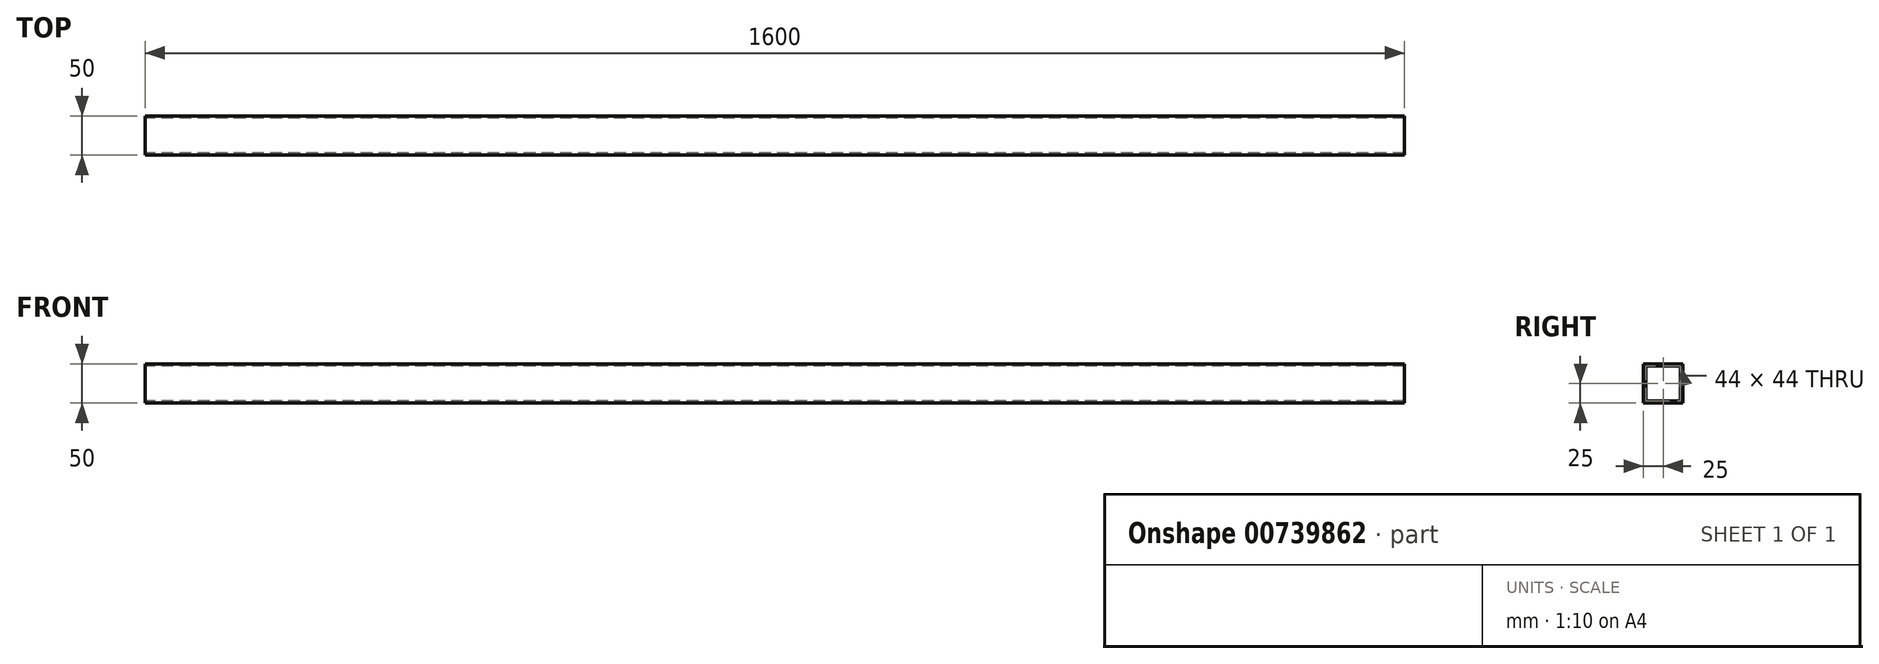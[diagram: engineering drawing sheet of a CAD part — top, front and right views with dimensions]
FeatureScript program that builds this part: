
annotation { "Feature Type Name" : "Feature", "Feature Type Description" : "" }
export const myFeature = defineFeature(function(context is Context, id is Id, definition is map)
    precondition{}
    {
        {
            var Q0;
            Q0=qCreatedBy(makeId("Right.planeOp"),FACE);
            var sketch = newSketch(context, id + "F0", { "sketchPlane" : qUnion([Q0])});
            skLineSegment(sketch, "E0.bottom", {"start": v(25, -25) * mm, "end": v(-25, -25) * mm});
            skLineSegment(sketch, "E0.top", {"start": v(25, 25) * mm, "end": v(-25, 25) * mm});
            skLineSegment(sketch, "E0.left", {"start": v(25, -25) * mm, "end": v(25, 25) * mm});
            skLineSegment(sketch, "E0.right", {"start": v(-25, -25) * mm, "end": v(-25, 25) * mm});
            skPoint(sketch, "E0.middle", {"position": v(0, 0) * mm});
            skLineSegment(sketch, "E1.0", {"start": v(22, 22) * mm, "end": v(-22, 22) * mm});
            skLineSegment(sketch, "E1.1", {"start": v(22, -22) * mm, "end": v(22, 22) * mm});
            skLineSegment(sketch, "E1.2", {"start": v(22, -22) * mm, "end": v(-22, -22) * mm});
            skLineSegment(sketch, "E1.3", {"start": v(-22, -22) * mm, "end": v(-22, 22) * mm});
            skSolve(sketch);
        }
        {
            var Q0;
            Q0 = qSketchRegion(id + "F0", true);
            extrude(context, id + "F1", {"entities" : qUnion([Q0]), "depth" : 1600 * mm, "offsetDistance" : 25 * mm});
        }
    });
